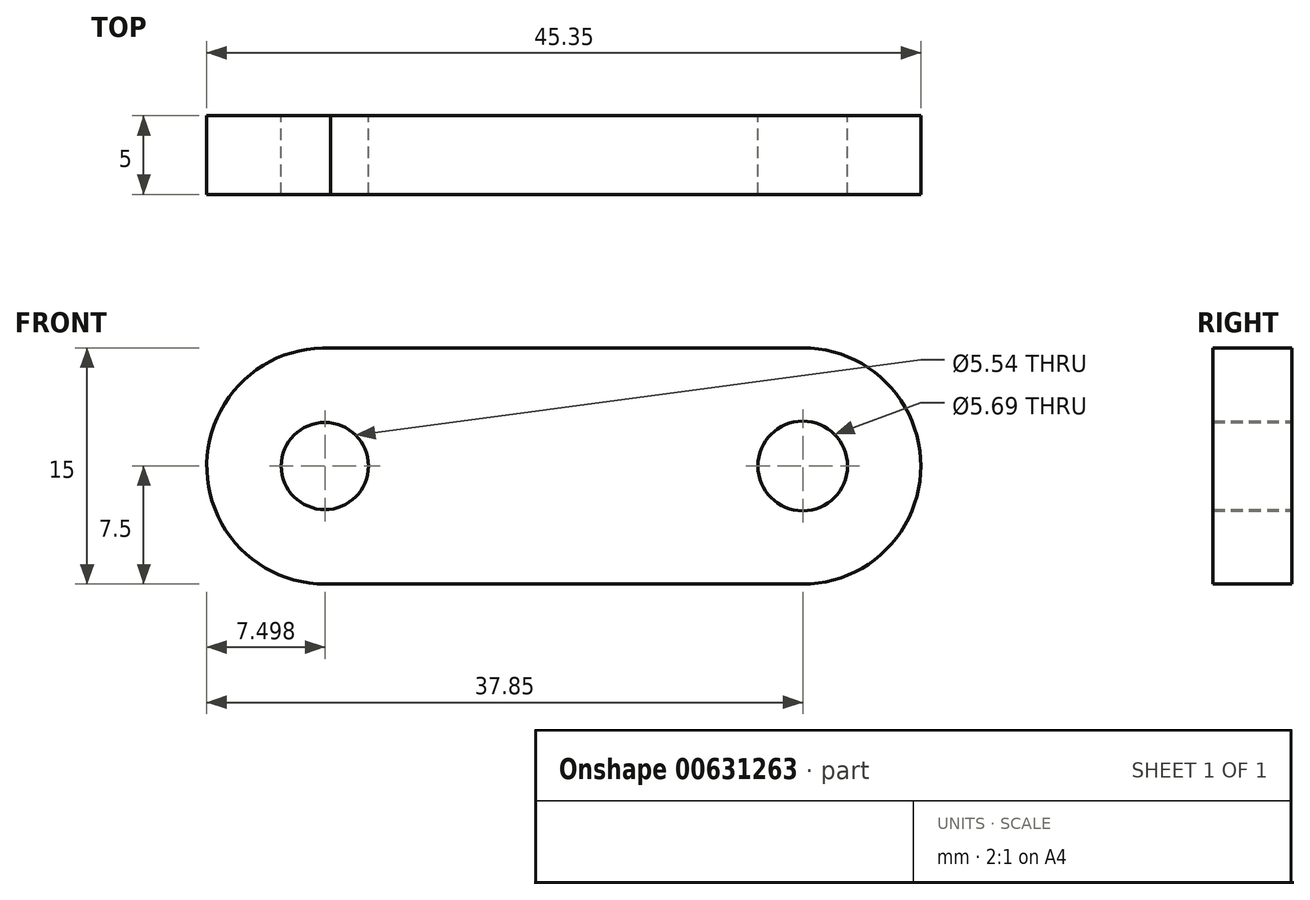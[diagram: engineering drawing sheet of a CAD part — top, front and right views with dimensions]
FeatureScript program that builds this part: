
annotation { "Feature Type Name" : "Feature", "Feature Type Description" : "" }
export const myFeature = defineFeature(function(context is Context, id is Id, definition is map)
    precondition{}
    {
        {
            var Q0;
            Q0=qCreatedBy(makeId("Front.planeOp"),FACE);
            var sketch = newSketch(context, id + "F0", { "sketchPlane" : qUnion([Q0])});
            skArc(sketch, "E0", {"start": v(-15, 7.5) * mm, "mid": v(-22.85, 0.17) * mm, "end": v(-15.35, -7.5) * mm});
            skArc(sketch, "E1", {"start": v(15, -7.5) * mm, "mid": v(22.5, 0) * mm, "end": v(15, 7.5) * mm});
            skLineSegment(sketch, "E2", {"start": v(-49.33, 0) * mm, "end": v(52.13, 0) * mm, "construction": true});
            skLineSegment(sketch, "E3", {"start": v(-15, 7.5) * mm, "end": v(15, 7.5) * mm});
            skLineSegment(sketch, "E4", {"start": v(-15.35, -7.5) * mm, "end": v(15, -7.5) * mm});
            skCircle(sketch, "E5", {"center": v(-15.35, 0) * mm, "radius": 2.77 * mm});
            skCircle(sketch, "E6", {"center": v(15, 0) * mm, "radius": 2.85 * mm});
            skSolve(sketch);
        }
        {
            var Q0;
            Q0 = qSketchRegion(id + "F0", true);
            extrude(context, id + "F1", {"entities" : qUnion([Q0]), "depth" : 5 * mm, "offsetDistance" : 25 * mm});
        }
    });
